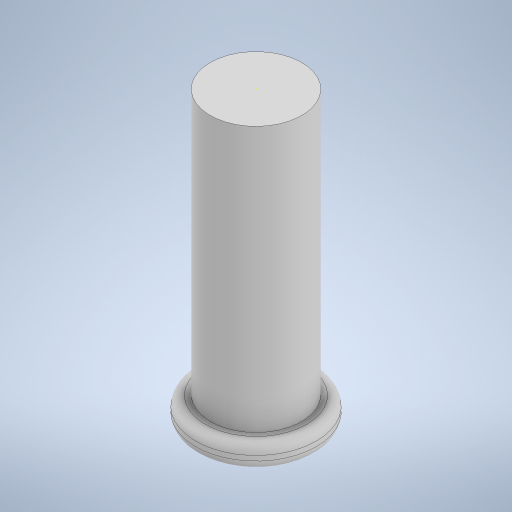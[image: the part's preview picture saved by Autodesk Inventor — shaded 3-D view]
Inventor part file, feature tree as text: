
AUTODESK INVENTOR PART (.ipt)
format: ipt  version: 2023 (Build 270158000, 158)  size: 257,024 bytes
history: native  units: mm
features: sketch x6, extrude x2, fillet x1
ambient origin geometry x8: Origin, YZ Plane, XZ Plane, XY Plane, X Axis, Y Axis, Z Axis, Center Point
bodies: Solid1 (feature_tree)
feature tree (9):
  extrude  "Extrusion1"  Depth=55.0mm TaperAngle=0.0deg
  sketch  "Sketch2"  dims[d3=25.0mm d4=5.0mm d5=0.0mm d6=2.0mm]
  extrude  "Extrusion2"  Depth=5.0mm TaperAngle=0.0deg
  fillet  "Fillet1"  Radius=2.0mm
  sketch  "Sketch4"
  sketch  "Sketch5"
  sketch  "Sketch6"
  sketch  "Sketch1"  dims[d0=19.0mm d1=55.0mm d2=0.0mm]
  sketch  "Sketch3"
